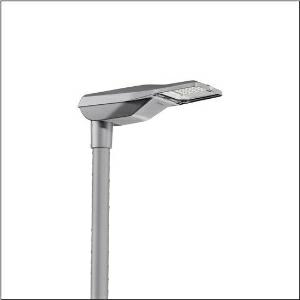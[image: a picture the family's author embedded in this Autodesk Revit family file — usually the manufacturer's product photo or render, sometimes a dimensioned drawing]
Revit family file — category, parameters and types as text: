
# Revit family: streetlight_sl_21_iq_micro___st0_8a_5xe1c41g08db_305a
name_source: partatom
category: Lighting Fixtures
units: mm (PartAtom-declared; Revit-internal decimal feet)

## family parameters
Cut with Voids When Loaded = No
Host = Face
Light Source = No
Part Type = Normal
Room Calculation Point = No
Round Connector Dimension = Use Diameter
Shared = No

## types (1)
- --- (1 x LED, 5010 lm, 36.4 W, 4000K)
    Apparent Load = 36 VA
    CIE Flux Codes = 38 75 97 100 100
    Color Rendering = 70
    Color Temperature = 4000K
    Default Elevation = 1800 mm
    Description = Streetlight SL 21 iQ micro, mast luminaire, primary light control with lens, of PMMA, primary optical cover: cover, of toughened safety glass, transparent, light distribution: ST0.8a, light emission: direct distribution, primary light characteristic: asymmetric, installation type: post-top, side-entry, LED, High Power LED, rated luminous flux: 5.010lm, luminous efficacy: 138lm/W, light colour: 740, colour temperature: 4000K, control gear: iQ Street-Remote, control: Street-Remote, Auto-Match, Temp-Guard, Lumen-Switch, Night-Set, Smart-Wire, Light-Fading, Desk-Remote (wireless, voltage-free reading and setting of iQ features in the workshop via application-optimized NFC function/RFID function), optimised constant luminous flux control (CLO 2.0), pre-setting: linear dimming characteristic, mains connection: 220..240V, AC, 50/60Hz, start of lifetime: 36W, end of service life: 38W, reduction: 16W, luminaire housing, of diecast aluminium, powder-coated, Siteco® metallic grey (DB 702S), corrosivity category C5 mid according to DIN EN ISO 12944, please order mast flange separately, inclination adjustable: 0°, 5°, 10°, 15°, sealing non-destructively replaceable, multi-level sealing system, length: 528mm, width: 235mm, height: 110mm, mast flange for spigot size: 42mm (side-entry): 5XC10008XM4, 60/48mm (side-entry/post-top): 5XC10108XM2, 76/60mm (side-entry/post-top): 5XC10108XM1, protection rating (complete): IP66, insulation class (complete): insulation class II (safety insulation), certification: CE, ENEC, ENEC+, VDE, impact resistance: IK10, permissible operating ambient temperature for outdoor applications: -40..+50°C, standard-compliant lighting for roads and squares, packaging unit: 1 piece

Light Distribution: ST0.8a
    Height = 110 mm
    Lamp = 1 x LED
    Lamp Light Flux = 5010 lm
    Lamp Power = 36.4 W
    Lamp count = 1
    Length = 528 mm
    Luminous efficacy = 138 lm/W
    Manufacturer = Siteco
    ModVariant = No
    Model = 5XE1C41G08DB
    Number of Poles = 1
    OnlyDefault = Yes
    Power Factor = 1
    Product Name = Streetlight SL 21 iQ micro | ST0.8a
    Product group = mast luminaire | pylon top
    ProductGroupID = 6100
    Protection Class = Protection class II
    Protection Degree = IP 66
    RLX_Detail_Level = 1
    RLX_Emergency_Light_Flux = 0 lm
    RLX_Emergency_Type = 0
    RLX_Emergency_Type_DB = No
    RlxData = <blob elided: 98725 chars, md5=0317a142>
    Socket = socket
    Standby Power = 0 W
    System Light Flux = 5010 lm
    System Power = 36 W
    Type Comments = factory setting: luminous flux: 100 % | dim-lin: 254 | 715 mA
    Type Image = l_1006881.jpg
    URL = http://relux.com
    VarID = @adj_154504
    Voltage = 0 V
    Weight = 0.00 kg
    Width = 235 mm

## geometry (parser evidence)
native form markers: Blend x4, Sweep x10
no freeform markers — native parametric forms only
